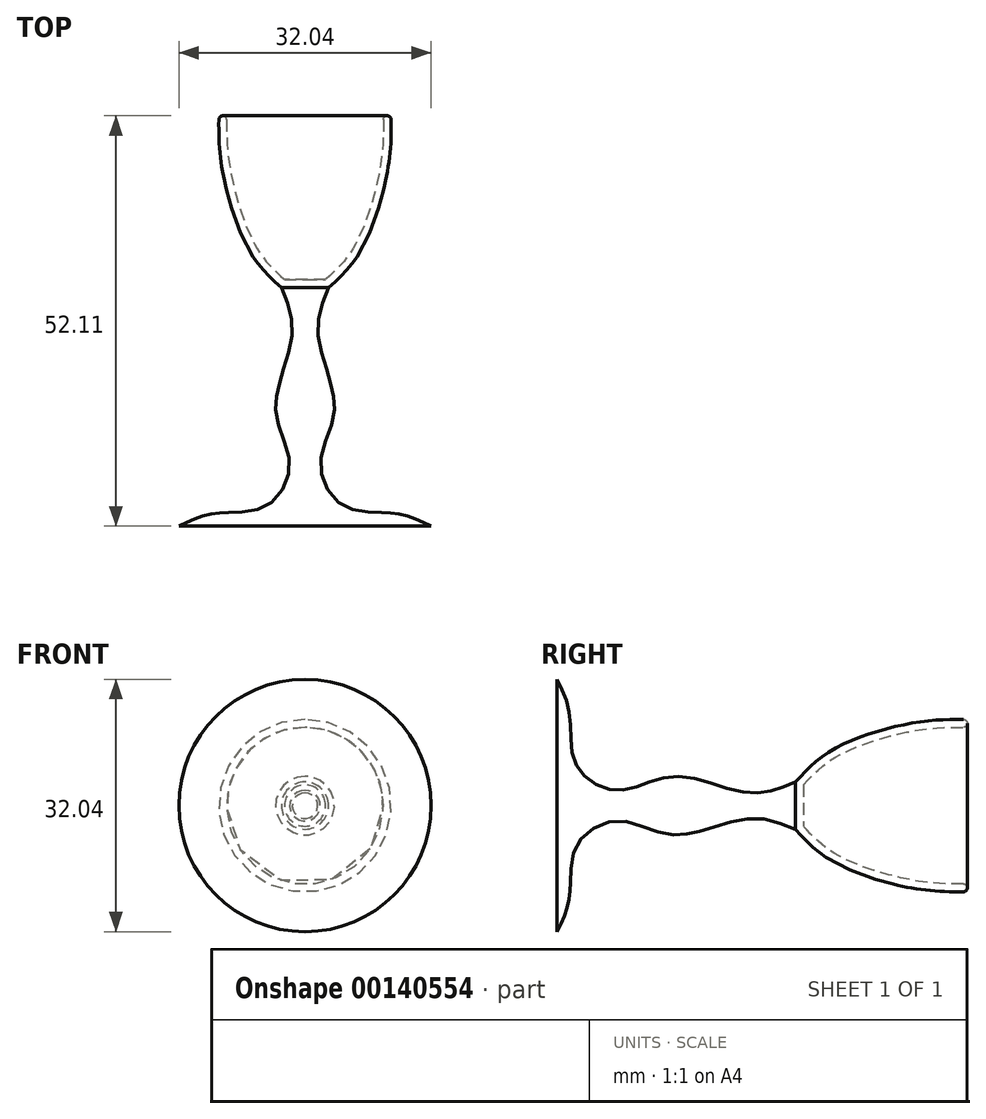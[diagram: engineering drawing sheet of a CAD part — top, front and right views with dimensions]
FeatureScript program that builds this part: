
annotation { "Feature Type Name" : "Feature", "Feature Type Description" : "" }
export const myFeature = defineFeature(function(context is Context, id is Id, definition is map)
    precondition{}
    {
        {
            var Q0;
            Q0=qCreatedBy(makeId("Top.planeOp"),FACE);
            var sketch = newSketch(context, id + "F0", { "sketchPlane" : qUnion([Q0])});
            skLineSegment(sketch, "E0", {"start": v(0, 0) * mm, "end": v(-3, 0) * mm});
            skLineSegment(sketch, "E1", {"start": v(0, 8.3) * mm, "end": v(0, 0) * mm});
            skFitSpline(sketch, "E2", {"points": [v(-3, 0) * mm, v(-6.5, 3.75) * mm, v(-9.46, 10.5) * mm, v(-10.81, 17.24) * mm, v(-10.95, 21.82) * mm], "startDerivative": vector(-15.82, 14.3) * mm, "endDerivative": vector(0.17, 19.93) * mm});
            skLineSegment(sketch, "E3", {"start": v(-10.95, 21.82) * mm, "end": v(0, 21.82) * mm});
            skLineSegment(sketch, "E4", {"start": v(0, 21.82) * mm, "end": v(0, 8.3) * mm});
            skSolve(sketch);
        }
        {
            var Q0;
            Q0=makeQuery(id+"F0.imprint","IMPRINT",FACE,{"disambiguationData":[TD([[makeQuery(id+"F0.imprint","IMPRINT",EDGE,{"derivedFrom":sQuery(id+"F0.wireOp",EDGE,"E0")}),-1.0]])]});
            var Q1;
            Q1=sQuery(id+"F0.wireOp",EDGE,"E1");
            revolve(context, id + "F1", {"entities" : qUnion([Q0]), "axis" : qUnion([Q1]), "revolveType" : RevolveType.FULL});
        }
        {
            var Q0;
            Q0=makeQuery(id+"F1.opRevolve","SWEPT_FACE",FACE,{"disambiguationData":[OSD([sQuery(id+"F0.wireOp",EDGE,"E3")])]});
            shell(context, id + "F2", {"entities" : qUnion([Q0]), "thickness" : 1 * mm});
        }
        {
            var Q0;
            Q0=makeQuery(id+"F1.opRevolve","SWEPT_EDGE",EDGE,{"disambiguationData":[OSD([sQuery(id+"F0.wireOp",EDGE,"E2"),sQuery(id+"F0.wireOp",EDGE,"E3")])]});
            var Q1;
            Q1=makeQuery(id+"F2.opShell","OFFSET_EDGE",EDGE,{"disambiguationData":[OSD([sQuery(id+"F0.wireOp",EDGE,"E2"),sQuery(id+"F0.wireOp",EDGE,"E3")])]});
            fillet(context, id + "F3", {"entities" : qUnion([Q0, Q1]), "radius" : .5 * mm, "tangentPropagation" : true, "allowEdgeOverflow" : false});
        }
        {
            var Q0;
            Q0=qCreatedBy(makeId("Top.planeOp"),FACE);
            var sketch = newSketch(context, id + "F4", { "sketchPlane" : qUnion([Q0])});
            skLineSegment(sketch, "E5.0", {"start": v(-3, 0) * mm, "end": v(3, 0) * mm});
            skLineSegment(sketch, "E6", {"start": v(0, 0) * mm, "end": v(0, -30.3) * mm});
            skLineSegment(sketch, "E7", {"start": v(0, -30.3) * mm, "end": v(16.02, -30.3) * mm});
            skFitSpline(sketch, "E8", {"points": [v(16.02, -30.3) * mm, v(11.5, -28.7) * mm, v(5.1, -27.83) * mm, v(1.96, -22.35) * mm, v(3.73, -15.48) * mm, v(1.67, -6.16) * mm, v(3, 0) * mm], "startDerivative": vector(-29.55, 14.72) * mm, "endDerivative": vector(14.63, 35.44) * mm});
            skSolve(sketch);
        }
        {
            var Q0;
            {var subQ2=sQuery(id+"F4.wireOp",EDGE,"E6");Q0=makeQuery(id+"F4.imprint","IMPRINT",FACE,{"disambiguationData":[TD([[makeQuery(id+"F4.imprint","IMPRINT",EDGE,{"derivedFrom":subQ2}),1.0]])]});}
            var Q1;
            Q1=sQuery(id+"F4.wireOp",EDGE,"E6");
            revolve(context, id + "F5", {"operationType" : NewBodyOperationType.ADD, "entities" : qUnion([Q0]), "axis" : qUnion([Q1]), "revolveType" : RevolveType.FULL});
        }
    });
